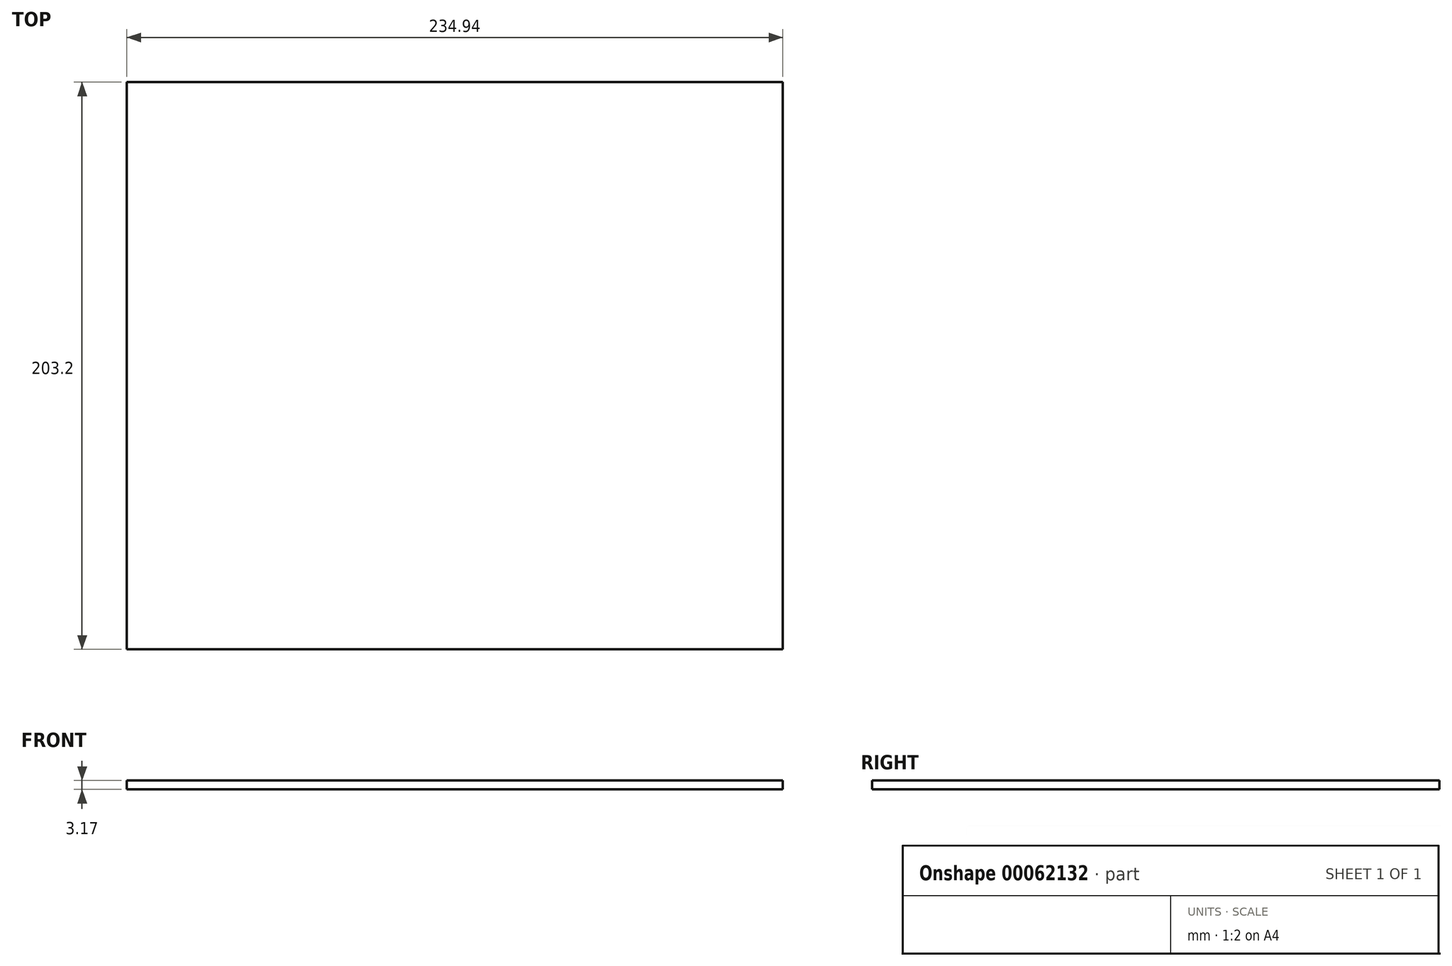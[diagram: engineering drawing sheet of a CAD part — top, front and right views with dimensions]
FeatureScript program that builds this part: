
annotation { "Feature Type Name" : "Feature", "Feature Type Description" : "" }
export const myFeature = defineFeature(function(context is Context, id is Id, definition is map)
    precondition{}
    {
        {
            var Q0;
            Q0=qCreatedBy(makeId("Top.planeOp"),FACE);
            var sketch = newSketch(context, id + "F0", { "sketchPlane" : qUnion([Q0])});
            skLineSegment(sketch, "E0.rect.bottom", {"start": v(117.47, 101.6) * mm, "end": v(-117.48, 101.6) * mm});
            skLineSegment(sketch, "E0.rect.top", {"start": v(117.48, -101.6) * mm, "end": v(-117.47, -101.6) * mm});
            skLineSegment(sketch, "E0.rect.left", {"start": v(117.47, 101.6) * mm, "end": v(117.48, -101.6) * mm});
            skLineSegment(sketch, "E0.rect.right", {"start": v(-117.48, 101.6) * mm, "end": v(-117.47, -101.6) * mm});
            skPoint(sketch, "E0.rect.middle", {"position": v(0, 0) * mm});
            skSolve(sketch);
        }
        {
            var Q0;
            Q0 = qSketchRegion(id + "F0", true);
            extrude(context, id + "F1", {"entities" : qUnion([Q0]), "depth" : 3.17 * mm});
        }
    });
